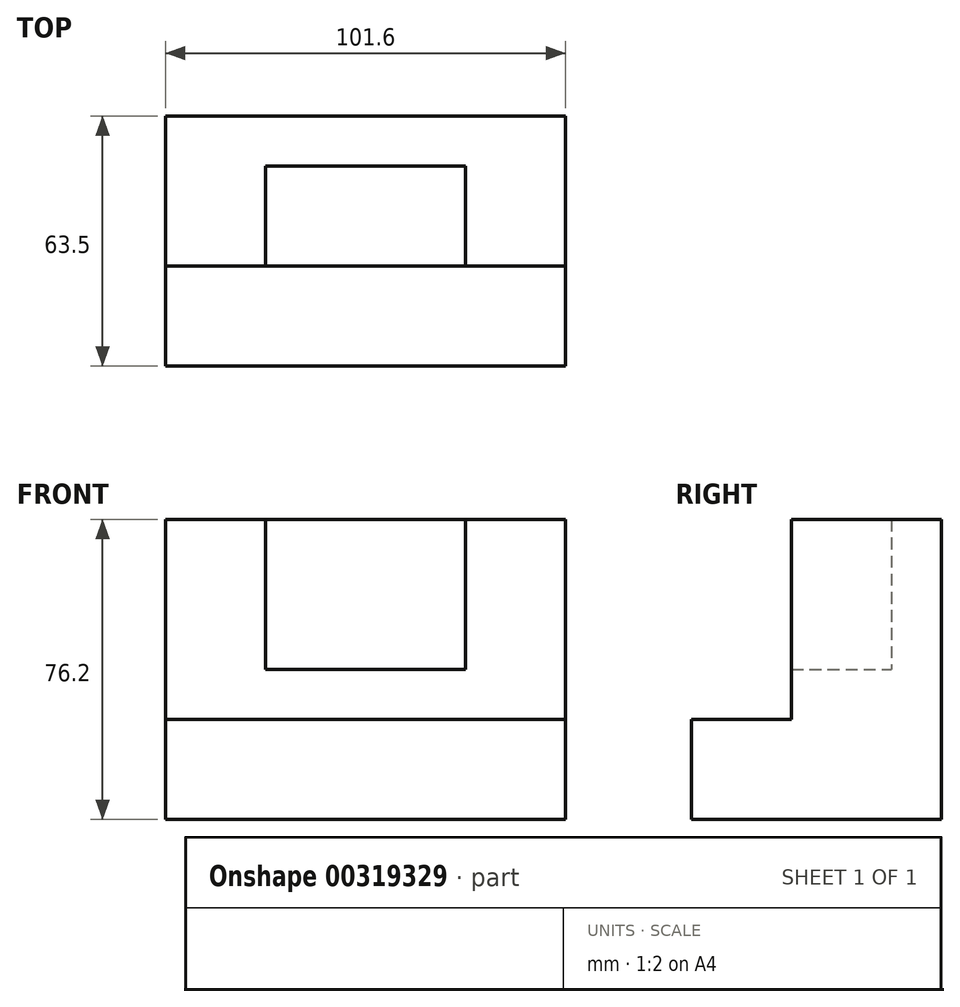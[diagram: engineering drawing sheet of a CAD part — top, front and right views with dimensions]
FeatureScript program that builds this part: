
annotation { "Feature Type Name" : "Feature", "Feature Type Description" : "" }
export const myFeature = defineFeature(function(context is Context, id is Id, definition is map)
    precondition{}
    {
        {
            var Q0;
            Q0=qCreatedBy(makeId("Top.planeOp"),FACE);
            var sketch = newSketch(context, id + "F0", { "sketchPlane" : qUnion([Q0])});
            skLineSegment(sketch, "E0.bottom", {"start": v(-30.59, 29.08) * mm, "end": v(71.01, 29.08) * mm});
            skLineSegment(sketch, "E0.top", {"start": v(-30.59, -34.42) * mm, "end": v(71.01, -34.42) * mm});
            skLineSegment(sketch, "E0.left", {"start": v(-30.59, 29.08) * mm, "end": v(-30.59, -34.42) * mm});
            skLineSegment(sketch, "E0.right", {"start": v(71.01, 29.08) * mm, "end": v(71.01, -34.42) * mm});
            skSolve(sketch);
        }
        {
            var Q0;
            Q0=makeQuery(id+"F0.imprint","IMPRINT",FACE,{"disambiguationData":[TD([[makeQuery(id+"F0.imprint","IMPRINT",EDGE,{"derivedFrom":sQuery(id+"F0.wireOp",EDGE,"E0.bottom")}),-1.0]])]});
            extrude(context, id + "F1", {"entities" : qUnion([Q0]), "depth" : 25.4 * mm});
        }
        {
            var Q0;
            Q0=makeQuery(id+"F1.opExtrude","CAP_FACE",FACE,{"disambiguationData":[OSD([sQuery(id+"F0.wireOp",EDGE,"E0.bottom"),sQuery(id+"F0.wireOp",EDGE,"E0.top"),sQuery(id+"F0.wireOp",EDGE,"E0.left"),sQuery(id+"F0.wireOp",EDGE,"E0.right")])],"isStart":false});
            var sketch = newSketch(context, id + "F2", { "sketchPlane" : qUnion([Q0])});
            skLineSegment(sketch, "E1", {"start": v(-30.59, -9.02) * mm, "end": v(-5.19, -9.02) * mm});
            skLineSegment(sketch, "E2", {"start": v(-5.19, -9.02) * mm, "end": v(-5.19, 16.38) * mm});
            skLineSegment(sketch, "E3", {"start": v(-5.19, 16.38) * mm, "end": v(45.61, 16.38) * mm});
            skLineSegment(sketch, "E4", {"start": v(45.61, 16.38) * mm, "end": v(45.61, -9.02) * mm});
            skLineSegment(sketch, "E5", {"start": v(45.61, -9.02) * mm, "end": v(71.01, -9.02) * mm});
            skLineSegment(sketch, "E6", {"start": v(71.01, -9.02) * mm, "end": v(71.01, 29.08) * mm});
            skLineSegment(sketch, "E7", {"start": v(71.01, 29.08) * mm, "end": v(-30.59, 29.08) * mm});
            skLineSegment(sketch, "E8", {"start": v(-30.59, 29.08) * mm, "end": v(-30.59, -9.02) * mm});
            skSolve(sketch);
        }
        {
            var Q0;
            Q0 = qSketchRegion(id + "F2", true);
            extrude(context, id + "F3", {"entities" : qUnion([Q0]), "operationType" : NewBodyOperationType.ADD, "depth" : 50.8 * mm});
        }
        {
            var Q0;
            Q0=makeQuery(id+"F1.opExtrude","CAP_FACE",FACE,{"disambiguationData":[OSD([sQuery(id+"F0.wireOp",EDGE,"E0.bottom"),sQuery(id+"F0.wireOp",EDGE,"E0.top"),sQuery(id+"F0.wireOp",EDGE,"E0.left"),sQuery(id+"F0.wireOp",EDGE,"E0.right")])],"isStart":false});
            var sketch = newSketch(context, id + "F4", { "sketchPlane" : qUnion([Q0])});
            skLineSegment(sketch, "E9", {"start": v(-5.19, -9.02) * mm, "end": v(45.61, -9.02) * mm});
            skLineSegment(sketch, "E10", {"start": v(45.61, -9.02) * mm, "end": v(45.61, 16.38) * mm});
            skLineSegment(sketch, "E11", {"start": v(45.61, 16.38) * mm, "end": v(-5.19, 16.38) * mm});
            skLineSegment(sketch, "E12", {"start": v(-5.19, 16.38) * mm, "end": v(-5.19, -9.02) * mm});
            skSolve(sketch);
        }
        {
            var Q0;
            Q0 = qSketchRegion(id + "F4", true);
            extrude(context, id + "F5", {"entities" : qUnion([Q0]), "operationType" : NewBodyOperationType.ADD, "depth" : 12.7 * mm});
        }
    });
